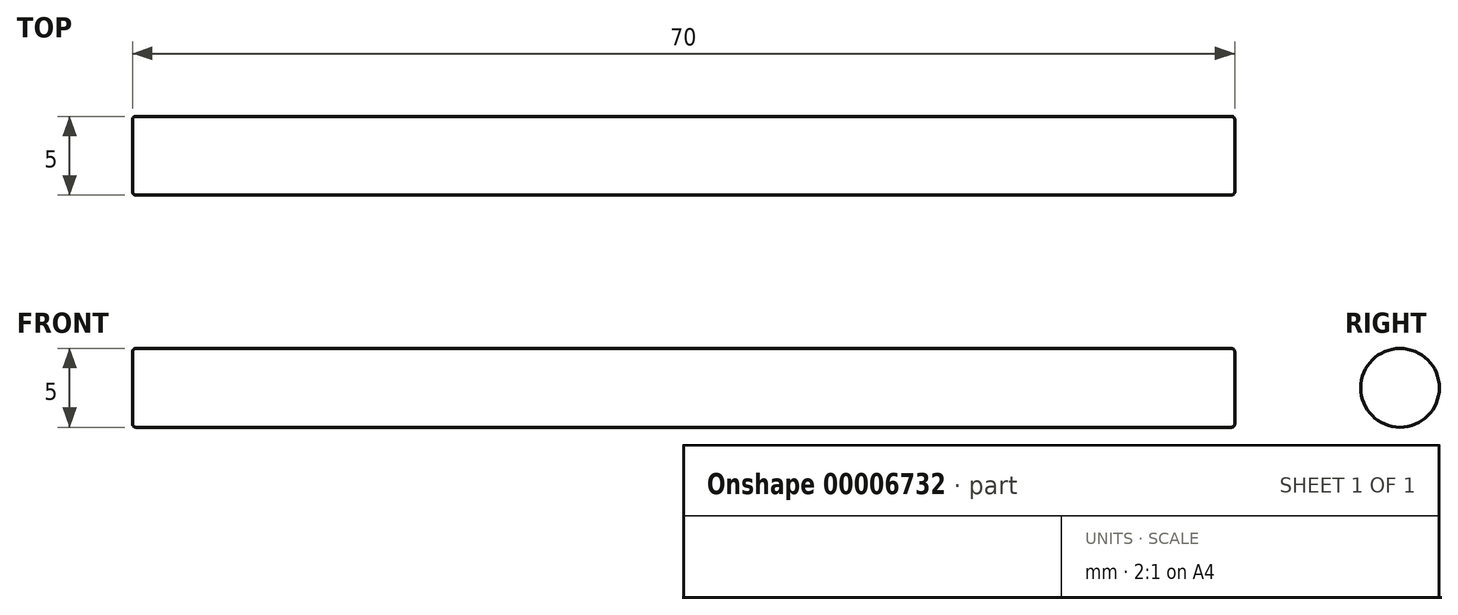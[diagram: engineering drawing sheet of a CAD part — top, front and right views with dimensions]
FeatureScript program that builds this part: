
annotation { "Feature Type Name" : "Feature", "Feature Type Description" : "" }
export const myFeature = defineFeature(function(context is Context, id is Id, definition is map)
    precondition{}
    {
        {
            var Q0;
            Q0=qCreatedBy(makeId("Right.planeOp"),FACE);
            var sketch = newSketch(context, id + "F0", { "sketchPlane" : qUnion([Q0])});
            skCircle(sketch, "E0", {"center": v(0, 0) * mm, "radius": 2.5 * mm});
            skSolve(sketch);
        }
        {
            var Q0;
            Q0 = qSketchRegion(id + "F0", true);
            extrude(context, id + "F1", {"entities" : qUnion([Q0]), "endBound" : BoundingType.SYMMETRIC, "depth" : 70 * mm});
        }
        {
            var Q0;
            Q0=makeQuery(id+"F1.opExtrude","CAP_EDGE",EDGE,{"disambiguationData":[OSD([sQuery(id+"F0.wireOp",EDGE,"E0")])],"isStart":false});
            var Q1;
            Q1=makeQuery(id+"F1.opExtrude","CAP_EDGE",EDGE,{"disambiguationData":[OSD([sQuery(id+"F0.wireOp",EDGE,"E0")])],"isStart":true});
            fillet(context, id + "F2", {"entities" : qUnion([Q0, Q1]), "radius" : 0.2 * mm, "tangentPropagation" : true, "allowEdgeOverflow" : false});
        }
    });
